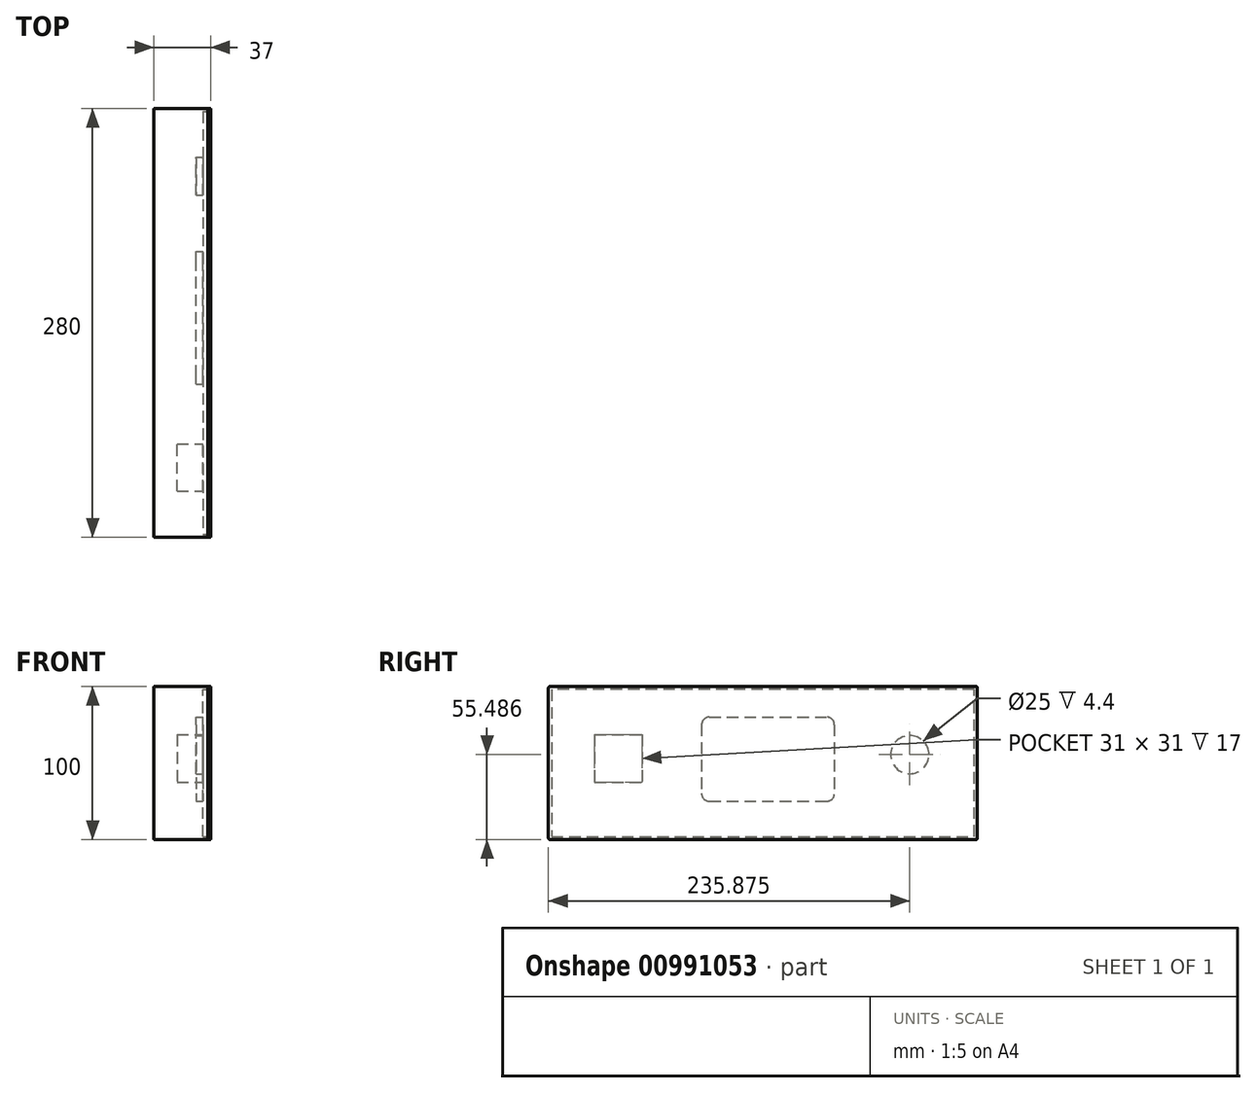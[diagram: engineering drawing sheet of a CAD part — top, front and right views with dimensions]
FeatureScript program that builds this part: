
annotation { "Feature Type Name" : "Feature", "Feature Type Description" : "" }
export const myFeature = defineFeature(function(context is Context, id is Id, definition is map)
    precondition{}
    {
        {
            var Q0;
            Q0=qCreatedBy(makeId("Right.planeOp"),FACE);
            var sketch = newSketch(context, id + "F0", { "sketchPlane" : qUnion([Q0])});
            skLineSegment(sketch, "E0.bottom", {"start": v(0, 0) * mm, "end": v(280, 0) * mm});
            skLineSegment(sketch, "E0.top", {"start": v(0, 100) * mm, "end": v(280, 100) * mm});
            skLineSegment(sketch, "E0.left", {"start": v(0, 0) * mm, "end": v(0, 100) * mm});
            skLineSegment(sketch, "E0.right", {"start": v(280, 0) * mm, "end": v(280, 100) * mm});
            skSolve(sketch);
        }
        {
            var Q0;
            Q0=makeQuery(id+"F0.imprint","IMPRINT",FACE,{"disambiguationData":[TD([[makeQuery(id+"F0.imprint","IMPRINT",EDGE,{"derivedFrom":sQuery(id+"F0.wireOp",EDGE,"E0.bottom")}),1.0]])]});
            extrude(context, id + "F1", {"entities" : qUnion([Q0]), "depth" : 35 * mm, "offsetDistance" : 25 * mm});
        }
        {
            var Q0;
            Q0=makeQuery(id+"F1.opExtrude","CAP_FACE",FACE,{"disambiguationData":[OSD([sQuery(id+"F0.wireOp",EDGE,"E0.bottom"),sQuery(id+"F0.wireOp",EDGE,"E0.top"),sQuery(id+"F0.wireOp",EDGE,"E0.left"),sQuery(id+"F0.wireOp",EDGE,"E0.right")])],"isStart":false});
            extrude(context, id + "F2", {"entities" : qUnion([Q0]), "depth" : 2 * mm, "offsetDistance" : 25 * mm});
        }
        {
            var Q0;
            Q0=makeQuery(id+"F1.opExtrude","SWEPT_EDGE",EDGE,{"disambiguationData":[OSD([sQuery(id+"F0.wireOp",EDGE,"E0.top"),sQuery(id+"F0.wireOp",EDGE,"E0.left")])]});
            var Q1;
            Q1=makeQuery(id+"F1.opExtrude","SWEPT_EDGE",EDGE,{"disambiguationData":[OSD([sQuery(id+"F0.wireOp",EDGE,"E0.bottom"),sQuery(id+"F0.wireOp",EDGE,"E0.left")])]});
            var Q2;
            Q2=makeQuery(id+"F1.opExtrude","SWEPT_EDGE",EDGE,{"disambiguationData":[OSD([sQuery(id+"F0.wireOp",EDGE,"E0.bottom"),sQuery(id+"F0.wireOp",EDGE,"E0.right")])]});
            var Q3;
            Q3=makeQuery(id+"F1.opExtrude","SWEPT_EDGE",EDGE,{"disambiguationData":[OSD([sQuery(id+"F0.wireOp",EDGE,"E0.top"),sQuery(id+"F0.wireOp",EDGE,"E0.right")])]});
            var Q4;
            Q4=makeQuery(id+"F2.opExtrude","SWEPT_EDGE",EDGE,{"disambiguationData":[OSD([sQuery(id+"F0.wireOp",EDGE,"E0.bottom"),sQuery(id+"F0.wireOp",EDGE,"E0.right")])]});
            var Q5;
            Q5=makeQuery(id+"F2.opExtrude","SWEPT_EDGE",EDGE,{"disambiguationData":[OSD([sQuery(id+"F0.wireOp",EDGE,"E0.top"),sQuery(id+"F0.wireOp",EDGE,"E0.right")])]});
            var Q6;
            Q6=makeQuery(id+"F2.opExtrude","SWEPT_EDGE",EDGE,{"disambiguationData":[OSD([sQuery(id+"F0.wireOp",EDGE,"E0.bottom"),sQuery(id+"F0.wireOp",EDGE,"E0.left")])]});
            var Q7;
            Q7=makeQuery(id+"F2.opExtrude","SWEPT_EDGE",EDGE,{"disambiguationData":[OSD([sQuery(id+"F0.wireOp",EDGE,"E0.top"),sQuery(id+"F0.wireOp",EDGE,"E0.left")])]});
            fillet(context, id + "F3", {"entities" : qUnion([Q0, Q1, Q2, Q3, Q4, Q5, Q6, Q7]), "radius" : 1 * mm, "tangentPropagation" : true, "allowEdgeOverflow" : false});
        }
        {
            var Q0;
            Q0=makeQuery(id+"F1.opExtrude","CAP_FACE",FACE,{"disambiguationData":[OSD([sQuery(id+"F0.wireOp",EDGE,"E0.bottom"),sQuery(id+"F0.wireOp",EDGE,"E0.top"),sQuery(id+"F0.wireOp",EDGE,"E0.left"),sQuery(id+"F0.wireOp",EDGE,"E0.right")])],"isStart":false});
            var sketch = newSketch(context, id + "F4", { "sketchPlane" : qUnion([Q0])});
            skLineSegment(sketch, "E1.bottom", {"start": v(100, 80) * mm, "end": v(186.7, 80) * mm});
            skLineSegment(sketch, "E1.top", {"start": v(100, 25) * mm, "end": v(186.7, 25) * mm});
            skLineSegment(sketch, "E1.left", {"start": v(100, 80) * mm, "end": v(100, 25) * mm});
            skLineSegment(sketch, "E1.right", {"start": v(186.7, 80) * mm, "end": v(186.7, 25) * mm});
            skLineSegment(sketch, "E2.bottom", {"start": v(30, 68.53) * mm, "end": v(61, 68.53) * mm});
            skLineSegment(sketch, "E2.top", {"start": v(30, 37.53) * mm, "end": v(61, 37.53) * mm});
            skLineSegment(sketch, "E2.left", {"start": v(30, 68.53) * mm, "end": v(30, 37.53) * mm});
            skLineSegment(sketch, "E2.right", {"start": v(61, 68.53) * mm, "end": v(61, 37.53) * mm});
            skCircle(sketch, "E3", {"center": v(235.87, 55.49) * mm, "radius": 12.5 * mm});
            skSolve(sketch);
        }
        {
            var Q0;
            Q0=makeQuery(id+"F4.imprint","IMPRINT",FACE,{"disambiguationData":[TD([[makeQuery(id+"F4.imprint","IMPRINT",EDGE,{"derivedFrom":sQuery(id+"F4.wireOp",EDGE,"E2.bottom")}),-1.0]])]});
            var Q1;
            Q1=makeQuery(id+"F4.imprint","IMPRINT",FACE,{"disambiguationData":[TD([[makeQuery(id+"F4.imprint","IMPRINT",EDGE,{"derivedFrom":sQuery(id+"F4.wireOp",EDGE,"E1.bottom")}),-1.0]])]});
            var Q2;
            Q2=makeQuery(id+"F4.imprint","IMPRINT",FACE,{"disambiguationData":[TD([[makeQuery(id+"F4.imprint","IMPRINT",EDGE,{"derivedFrom":sQuery(id+"F4.wireOp",EDGE,"E3")}),1.0]])]});
            extrude(context, id + "F5", {"entities" : qUnion([Q0, Q1, Q2]), "operationType" : NewBodyOperationType.REMOVE, "oppositeDirection" : true, "depth" : 20 * mm, "offsetDistance" : 25 * mm});
        }
        {
            var Q0;
            Q0=makeQuery(id+"F1.opExtrude","CAP_FACE",FACE,{"disambiguationData":[OSD([sQuery(id+"F0.wireOp",EDGE,"E0.bottom"),sQuery(id+"F0.wireOp",EDGE,"E0.top"),sQuery(id+"F0.wireOp",EDGE,"E0.left"),sQuery(id+"F0.wireOp",EDGE,"E0.right")])],"isStart":false});
            var sketch = newSketch(context, id + "F6", { "sketchPlane" : qUnion([Q0])});
            skLineSegment(sketch, "E4.0", {"start": v(278, 98) * mm, "end": v(2, 98) * mm});
            skLineSegment(sketch, "E4.1", {"start": v(278, 2) * mm, "end": v(278, 98) * mm});
            skLineSegment(sketch, "E4.2", {"start": v(2, 2) * mm, "end": v(278, 2) * mm});
            skLineSegment(sketch, "E4.3", {"start": v(2, 98) * mm, "end": v(2, 2) * mm});
            skSolve(sketch);
        }
        {
            var Q0;
            Q0=makeQuery(id+"F6.imprint","IMPRINT",FACE,{"disambiguationData":[TD([[makeQuery(id+"F6.imprint","IMPRINT",EDGE,{"derivedFrom":sQuery(id+"F6.wireOp",EDGE,"E4.0")}),1.0]])]});
            extrude(context, id + "F7", {"entities" : qUnion([Q0]), "operationType" : NewBodyOperationType.REMOVE, "oppositeDirection" : true, "depth" : 3 * mm, "offsetDistance" : 25 * mm});
        }
        {
            var Q0;
            Q0=makeQuery(id+"F5.boolean.opBoolean","COPY",EDGE,{"derivedFrom":makeQuery(id+"F5.opExtrude","SWEPT_EDGE",EDGE,{"disambiguationData":[OSD([sQuery(id+"F4.wireOp",EDGE,"E1.bottom"),sQuery(id+"F4.wireOp",EDGE,"E1.left")])]})});
            var Q1;
            Q1=makeQuery(id+"F5.boolean.opBoolean","COPY",EDGE,{"derivedFrom":makeQuery(id+"F5.opExtrude","SWEPT_EDGE",EDGE,{"disambiguationData":[OSD([sQuery(id+"F4.wireOp",EDGE,"E1.bottom"),sQuery(id+"F4.wireOp",EDGE,"E1.right")])]})});
            var Q2;
            Q2=makeQuery(id+"F5.boolean.opBoolean","COPY",EDGE,{"derivedFrom":makeQuery(id+"F5.opExtrude","SWEPT_EDGE",EDGE,{"disambiguationData":[OSD([sQuery(id+"F4.wireOp",EDGE,"E1.top"),sQuery(id+"F4.wireOp",EDGE,"E1.right")])]})});
            var Q3;
            Q3=makeQuery(id+"F5.boolean.opBoolean","COPY",EDGE,{"derivedFrom":makeQuery(id+"F5.opExtrude","SWEPT_EDGE",EDGE,{"disambiguationData":[OSD([sQuery(id+"F4.wireOp",EDGE,"E1.top"),sQuery(id+"F4.wireOp",EDGE,"E1.left")])]})});
            fillet(context, id + "F8", {"entities" : qUnion([Q0, Q1, Q2, Q3]), "radius" : 5 * mm, "tangentPropagation" : true, "allowEdgeOverflow" : false});
        }
        {
            var Q0;
            Q0=makeQuery(id+"F5.boolean.opBoolean","COPY",FACE,{"derivedFrom":makeQuery(id+"F5.opExtrude","CAP_FACE",FACE,{"disambiguationData":[OSD([sQuery(id+"F4.wireOp",EDGE,"E1.bottom"),sQuery(id+"F4.wireOp",EDGE,"E1.top"),sQuery(id+"F4.wireOp",EDGE,"E1.left"),sQuery(id+"F4.wireOp",EDGE,"E1.right")])],"isStart":false})});
            var Q1;
            Q1=makeQuery(id+"F5.boolean.opBoolean","COPY",FACE,{"derivedFrom":makeQuery(id+"F5.opExtrude","CAP_FACE",FACE,{"disambiguationData":[OSD([sQuery(id+"F4.wireOp",EDGE,"E3")])],"isStart":false})});
            extrude(context, id + "F9", {"entities" : qUnion([Q0, Q1]), "operationType" : NewBodyOperationType.ADD, "depth" : 12.6 * mm, "offsetDistance" : 25 * mm});
        }
    });
